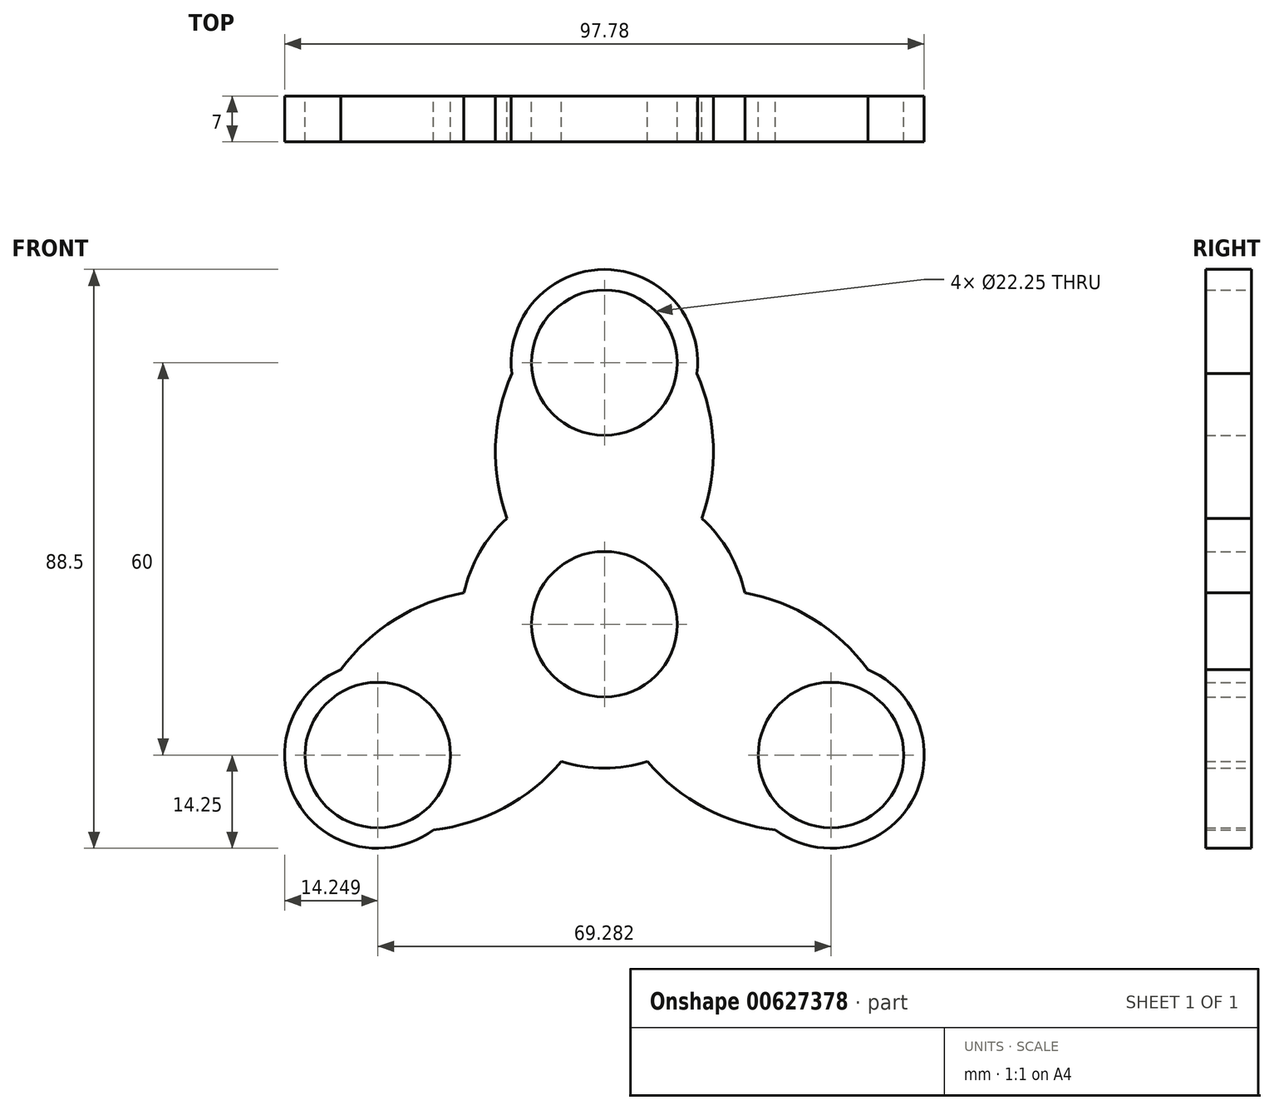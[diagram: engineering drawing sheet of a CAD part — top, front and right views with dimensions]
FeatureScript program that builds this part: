
annotation { "Feature Type Name" : "Feature", "Feature Type Description" : "" }
export const myFeature = defineFeature(function(context is Context, id is Id, definition is map)
    precondition{}
    {
        {
            var Q0;
            Q0=qCreatedBy(makeId("Front.planeOp"),FACE);
            var sketch = newSketch(context, id + "F0", { "sketchPlane" : qUnion([Q0])});
            skCircle(sketch, "E0", {"center": v(0, 0) * mm, "radius": 11.12 * mm});
            skCircle(sketch, "E1", {"center": v(0, 0) * mm, "radius": 13.5 * mm});
            skCircle(sketch, "E2", {"center": v(-34.64, -20) * mm, "radius": 11.12 * mm});
            skCircle(sketch, "E3", {"center": v(34.64, -20) * mm, "radius": 11.12 * mm});
            skCircle(sketch, "E4", {"center": v(0, 40) * mm, "radius": 11.12 * mm});
            skCircle(sketch, "E5", {"center": v(0, 40) * mm, "radius": 14.25 * mm});
            skCircle(sketch, "E6", {"center": v(-34.64, -20) * mm, "radius": 14.25 * mm});
            skCircle(sketch, "E7", {"center": v(34.64, -20) * mm, "radius": 14.25 * mm});
            skArc(sketch, "E8", {"start": v(10.63, 8.32) * mm, "mid": v(0, 16.5) * mm, "end": v(-10.63, 8.32) * mm});
            skArc(sketch, "E9", {"start": v(-12.52, 5.05) * mm, "mid": v(-14.29, -8.25) * mm, "end": v(-1.89, -13.37) * mm});
            skArc(sketch, "E10", {"start": v(1.89, -13.37) * mm, "mid": v(14.29, -8.25) * mm, "end": v(12.52, 5.05) * mm});
            skArc(sketch, "E11", {"start": v(-12.52, 5.05) * mm, "mid": v(-28.02, 2.82) * mm, "end": v(-40.28, -6.91) * mm});
            skArc(sketch, "E12", {"start": v(-26.13, -31.43) * mm, "mid": v(-11.56, -25.69) * mm, "end": v(-1.89, -13.37) * mm});
            skArc(sketch, "E13.1.0", {"start": v(1.89, -13.37) * mm, "mid": v(11.56, -25.68) * mm, "end": v(26.13, -31.43) * mm});
            skArc(sketch, "E13.1.1", {"start": v(40.28, -6.91) * mm, "mid": v(28.02, 2.83) * mm, "end": v(12.52, 5.05) * mm});
            skArc(sketch, "E13.2.0", {"start": v(10.63, 8.32) * mm, "mid": v(16.45, 22.85) * mm, "end": v(14.15, 38.34) * mm});
            skArc(sketch, "E13.2.1", {"start": v(-14.15, 38.34) * mm, "mid": v(-16.47, 22.85) * mm, "end": v(-10.63, 8.32) * mm});
            skArc(sketch, "E14", {"start": v(-14.9, 16.19) * mm, "mid": v(-19.06, 11) * mm, "end": v(-21.47, 4.8) * mm});
            skArc(sketch, "E15.trimOffspring", {"start": v(21.47, 4.8) * mm, "mid": v(19.05, 11) * mm, "end": v(14.89, 16.2) * mm});
            skArc(sketch, "E16.trimOffspring", {"start": v(-6.57, -21) * mm, "mid": v(0, -22) * mm, "end": v(6.58, -21) * mm});
            skSolve(sketch);
        }
        {
            var Q0;
            {var subQ4=sQuery(id+"F0.wireOp",EDGE,"E8");Q0=makeQuery(id+"F0.imprint","IMPRINT",FACE,{"disambiguationData":[TD([[makeQuery(id+"F0.imprint","IMPRINT",EDGE,{"derivedFrom":subQ4}),-1.0]])]});}
            var Q1;
            {var subQ5=sQuery(id+"F0.wireOp",EDGE,"E14");Q1=makeQuery(id+"F0.imprint","IMPRINT",FACE,{"disambiguationData":[TD([[makeQuery(id+"F0.imprint","IMPRINT",EDGE,{"derivedFrom":subQ5}),1.0]])]});}
            var Q2;
            {var subQ4=sQuery(id+"F0.wireOp",EDGE,"E9");Q2=makeQuery(id+"F0.imprint","IMPRINT",FACE,{"disambiguationData":[TD([[makeQuery(id+"F0.imprint","IMPRINT",EDGE,{"derivedFrom":subQ4}),-1.0]])]});}
            var Q3;
            {var subQ5=sQuery(id+"F0.wireOp",EDGE,"E16.trimOffspring");Q3=makeQuery(id+"F0.imprint","IMPRINT",FACE,{"disambiguationData":[TD([[makeQuery(id+"F0.imprint","IMPRINT",EDGE,{"derivedFrom":subQ5}),1.0]])]});}
            var Q4;
            {var subQ1=sQuery(id+"F0.wireOp",EDGE,"E10");Q4=makeQuery(id+"F0.imprint","IMPRINT",FACE,{"disambiguationData":[TD([[makeQuery(id+"F0.imprint","IMPRINT",EDGE,{"derivedFrom":subQ1}),-1.0]])]});}
            var Q5;
            {var subQ0=sQuery(id+"F0.wireOp",EDGE,"E10");Q5=makeQuery(id+"F0.imprint","IMPRINT",FACE,{"disambiguationData":[TD([[makeQuery(id+"F0.imprint","IMPRINT",EDGE,{"derivedFrom":subQ0}),1.0]])]});}
            var Q6;
            Q6=makeQuery(id+"F0.imprint","IMPRINT",FACE,{"disambiguationData":[TD([[makeQuery(id+"F0.imprint","IMPRINT",EDGE,{"derivedFrom":sQuery(id+"F0.wireOp",EDGE,"E0")}),-1.0]])]});
            var Q7;
            {var subQ0=sQuery(id+"F0.wireOp",EDGE,"E9");Q7=makeQuery(id+"F0.imprint","IMPRINT",FACE,{"disambiguationData":[TD([[makeQuery(id+"F0.imprint","IMPRINT",EDGE,{"derivedFrom":subQ0}),1.0]])]});}
            var Q8;
            {var subQ0=sQuery(id+"F0.wireOp",EDGE,"E8");Q8=makeQuery(id+"F0.imprint","IMPRINT",FACE,{"disambiguationData":[TD([[makeQuery(id+"F0.imprint","IMPRINT",EDGE,{"derivedFrom":subQ0}),1.0]])]});}
            var Q9;
            Q9=makeQuery(id+"F0.imprint","IMPRINT",FACE,{"disambiguationData":[TD([[makeQuery(id+"F0.imprint","IMPRINT",EDGE,{"derivedFrom":sQuery(id+"F0.wireOp",EDGE,"E4")}),-1.0]])]});
            var Q10;
            {var subQ5=sQuery(id+"F0.wireOp",EDGE,"E15.trimOffspring");Q10=makeQuery(id+"F0.imprint","IMPRINT",FACE,{"disambiguationData":[TD([[makeQuery(id+"F0.imprint","IMPRINT",EDGE,{"derivedFrom":subQ5}),1.0]])]});}
            var Q11;
            Q11=makeQuery(id+"F0.imprint","IMPRINT",FACE,{"disambiguationData":[TD([[makeQuery(id+"F0.imprint","IMPRINT",EDGE,{"derivedFrom":sQuery(id+"F0.wireOp",EDGE,"E3")}),-1.0]])]});
            var Q12;
            Q12=makeQuery(id+"F0.imprint","IMPRINT",FACE,{"disambiguationData":[TD([[makeQuery(id+"F0.imprint","IMPRINT",EDGE,{"derivedFrom":sQuery(id+"F0.wireOp",EDGE,"E2")}),-1.0]])]});
            extrude(context, id + "F1", {"entities" : qUnion([Q0, Q1, Q2, Q3, Q4, Q5, Q6, Q7, Q8, Q9, Q10, Q11, Q12]), "depth" : 7 * mm, "offsetDistance" : 25 * mm});
        }
    });
